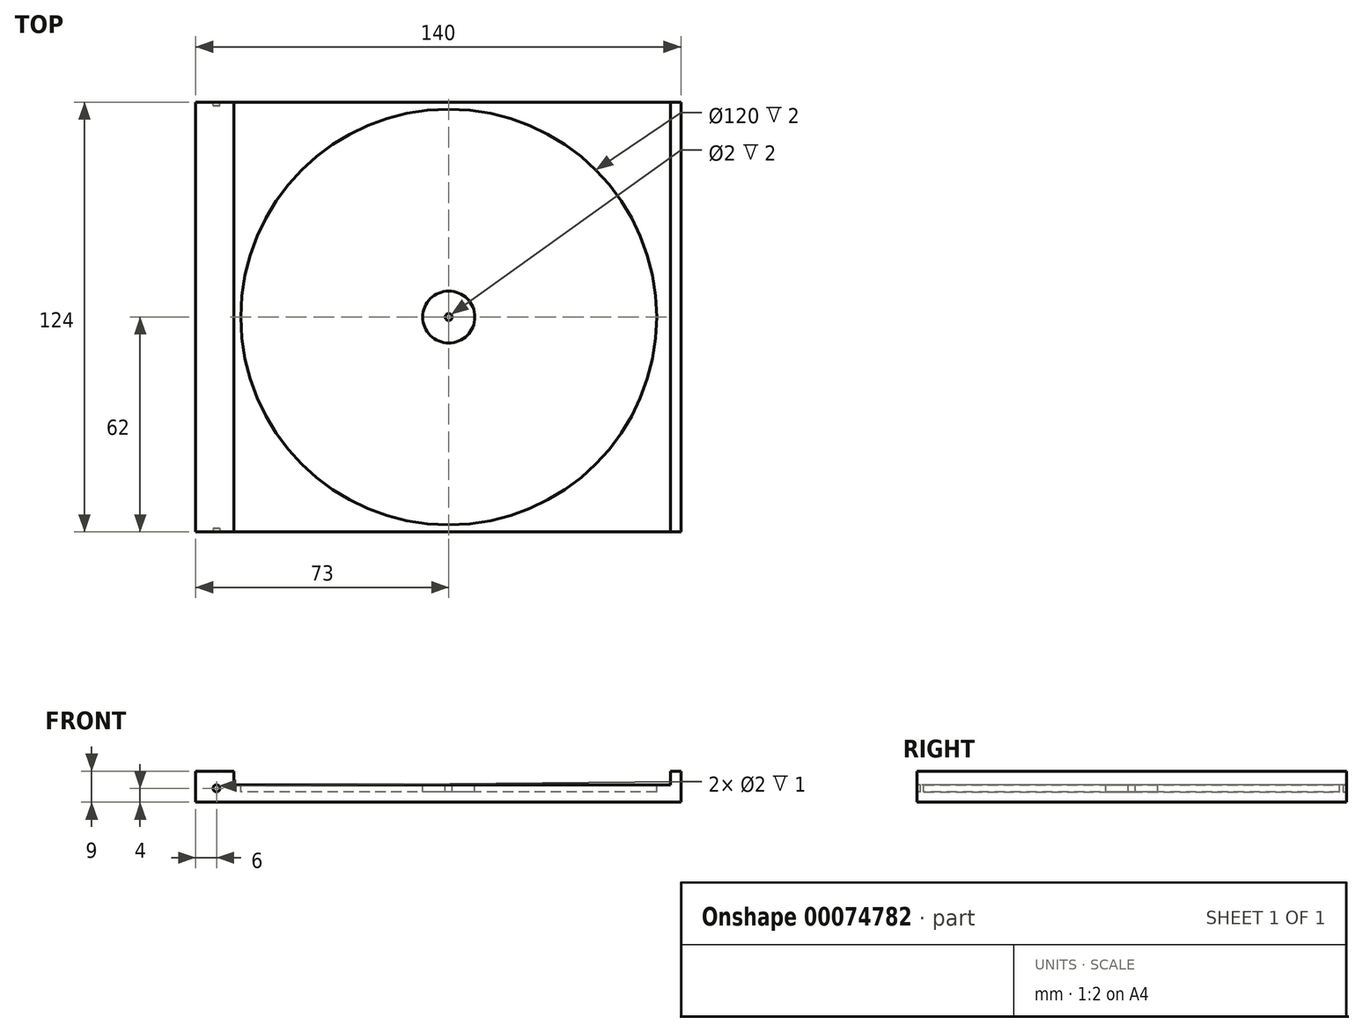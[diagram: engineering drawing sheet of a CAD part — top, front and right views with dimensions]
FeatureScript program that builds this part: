
annotation { "Feature Type Name" : "Feature", "Feature Type Description" : "" }
export const myFeature = defineFeature(function(context is Context, id is Id, definition is map)
    precondition{}
    {
        {
            var Q0;
            Q0=qCreatedBy(makeId("Top.planeOp"),FACE);
            var sketch = newSketch(context, id + "F0", { "sketchPlane" : qUnion([Q0])});
            skLineSegment(sketch, "E0.rect.bottom", {"start": v(-70, 62) * mm, "end": v(70, 62) * mm});
            skLineSegment(sketch, "E0.rect.top", {"start": v(-70, -62) * mm, "end": v(70, -62) * mm});
            skLineSegment(sketch, "E0.rect.left", {"start": v(-70, 62) * mm, "end": v(-70, -62) * mm});
            skLineSegment(sketch, "E0.rect.right", {"start": v(70, 62) * mm, "end": v(70, -62) * mm});
            skPoint(sketch, "E0.rect.middle", {"position": v(0, 0) * mm});
            skSolve(sketch);
        }
        {
            var Q0;
            Q0 = qSketchRegion(id + "F0", true);
            extrude(context, id + "F1", {"entities" : qUnion([Q0]), "oppositeDirection" : true, "depth" : 5 * mm});
        }
        {
            var Q0;
            Q0=makeQuery(id+"F1.opExtrude","CAP_FACE",FACE,{"disambiguationData":[OSD([sQuery(id+"F0.wireOp",EDGE,"E0.rect.bottom"),sQuery(id+"F0.wireOp",EDGE,"E0.rect.top"),sQuery(id+"F0.wireOp",EDGE,"E0.rect.left"),sQuery(id+"F0.wireOp",EDGE,"E0.rect.right")])],"isStart":true});
            var sketch = newSketch(context, id + "F2", { "sketchPlane" : qUnion([Q0])});
            skLineSegment(sketch, "E1", {"start": v(-59, -62) * mm, "end": v(-59, 62) * mm});
            skLineSegment(sketch, "E2", {"start": v(67, 62) * mm, "end": v(67, -62) * mm});
            skPoint(sketch, "E3.endSnap0", {"position": v(70, 0) * mm});
            skLineSegment(sketch, "E4", {"start": v(-59, 62) * mm, "end": v(-70, 62) * mm});
            skLineSegment(sketch, "E5", {"start": v(-70, 62) * mm, "end": v(-70, -62) * mm});
            skLineSegment(sketch, "E6", {"start": v(-70, -62) * mm, "end": v(-59, -62) * mm});
            skLineSegment(sketch, "E7", {"start": v(67, 62) * mm, "end": v(70, 62) * mm});
            skLineSegment(sketch, "E8", {"start": v(70, 62) * mm, "end": v(70, -62) * mm});
            skLineSegment(sketch, "E9", {"start": v(70, -62) * mm, "end": v(67, -62) * mm});
            skSolve(sketch);
        }
        {
            var Q0;
            Q0 = qSketchRegion(id + "F2", true);
            extrude(context, id + "F3", {"entities" : qUnion([Q0]), "operationType" : NewBodyOperationType.ADD, "depth" : 4 * mm});
        }
        {
            var Q0;
            Q0=makeQuery(id+"F1.opExtrude","CAP_FACE",FACE,{"disambiguationData":[OSD([sQuery(id+"F0.wireOp",EDGE,"E0.rect.bottom"),sQuery(id+"F0.wireOp",EDGE,"E0.rect.top"),sQuery(id+"F0.wireOp",EDGE,"E0.rect.left"),sQuery(id+"F0.wireOp",EDGE,"E0.rect.right")])],"isStart":true});
            var sketch = newSketch(context, id + "F4", { "sketchPlane" : qUnion([Q0])});
            skLineSegment(sketch, "E10.0", {"start": v(-59, 0) * mm, "end": v(67, 0) * mm});
            skLineSegment(sketch, "E11.0", {"start": v(3, 62) * mm, "end": v(3, -62) * mm});
            skCircle(sketch, "E12", {"center": v(3, 0) * mm, "radius": 60 * mm});
            skCircle(sketch, "E13", {"center": v(3, 0) * mm, "radius": 7.5 * mm});
            skCircle(sketch, "E14", {"center": v(3, 0) * mm, "radius": 1 * mm});
            skSolve(sketch);
        }
        {
            var Q0;
            Q0 = qSketchRegion(id + "F4", true);
            extrude(context, id + "F5", {"entities" : qUnion([Q0]), "operationType" : NewBodyOperationType.REMOVE, "flatOperationType" : FlatOperationType.REMOVE, "oppositeDirection" : true, "offsetDistance" : 25 * mm, "depth" : 2 * mm, "domain" : OperationDomain.MODEL});
        }
        {
            var Q0;
            {var subQ0=sQuery(id+"F4.wireOp",EDGE,"E11.0");var subQ1=sQuery(id+"F4.wireOp",EDGE,"E10.0");var subQ2=makeQuery(id+"F4.imprint","INTERSECT",VERTEX,{"derivedFrom":[subQ1,subQ0]});Q0=makeQuery(id+"F4.imprint","IMPRINT",FACE,{"disambiguationData":[TD([[makeQuery(id+"F4.imprint","IMPRINT",EDGE,{"disambiguationData":[TD([[subQ2,-1.0]])],"derivedFrom":subQ1}),-1.0]])]});}
            var Q1;
            {var subQ0=sQuery(id+"F4.wireOp",EDGE,"E14");var subQ1=sQuery(id+"F4.wireOp",EDGE,"E10.0");var subQ2=makeQuery(id+"F4.imprint","INTERSECT",VERTEX,{"disambiguationData":[OD(0.0)],"derivedFrom":[subQ1,subQ0]});Q1=makeQuery(id+"F4.imprint","IMPRINT",FACE,{"disambiguationData":[TD([[makeQuery(id+"F4.imprint","IMPRINT",EDGE,{"disambiguationData":[TD([[subQ2,-1.0]])],"derivedFrom":subQ1}),-1.0]])]});}
            var Q2;
            {var subQ0=sQuery(id+"F4.wireOp",EDGE,"E14");var subQ1=sQuery(id+"F4.wireOp",EDGE,"E10.0");var subQ2=makeQuery(id+"F4.imprint","INTERSECT",VERTEX,{"disambiguationData":[OD(0.0)],"derivedFrom":[subQ1,subQ0]});Q2=makeQuery(id+"F4.imprint","IMPRINT",FACE,{"disambiguationData":[TD([[makeQuery(id+"F4.imprint","IMPRINT",EDGE,{"disambiguationData":[TD([[subQ2,-1.0]])],"derivedFrom":subQ1}),1.0]])]});}
            var Q3;
            {var subQ0=sQuery(id+"F4.wireOp",EDGE,"E11.0");var subQ1=sQuery(id+"F4.wireOp",EDGE,"E10.0");var subQ2=makeQuery(id+"F4.imprint","INTERSECT",VERTEX,{"derivedFrom":[subQ1,subQ0]});Q3=makeQuery(id+"F4.imprint","IMPRINT",FACE,{"disambiguationData":[TD([[makeQuery(id+"F4.imprint","IMPRINT",EDGE,{"disambiguationData":[TD([[subQ2,-1.0]])],"derivedFrom":subQ1}),1.0]])]});}
            var Q4;
            Q4=sQuery(id+"F4.wireOp",EDGE,"E14");
            extrude(context, id + "F6", {"entities" : qUnion([Q0, Q1, Q2, Q3]), "operationType" : NewBodyOperationType.REMOVE, "surfaceEntities" : qUnion([Q4]), "oppositeDirection" : true, "depth" : 2 * mm});
        }
        {
            var Q0;
            Q0=makeQuery(id+"F3.boolean.opBoolean","MERGE",FACE,{"derivedFrom":[makeQuery(id+"F1.opExtrude","SWEPT_FACE",FACE,{"disambiguationData":[OSD([sQuery(id+"F0.wireOp",EDGE,"E0.rect.bottom")])]}),makeQuery(id+"F3.opExtrude","SWEPT_FACE",FACE,{"disambiguationData":[OSD([sQuery(id+"F2.wireOp",EDGE,"E4")])]}),makeQuery(id+"F3.opExtrude","SWEPT_FACE",FACE,{"disambiguationData":[OSD([sQuery(id+"F2.wireOp",EDGE,"E7")])]})]});
            var sketch = newSketch(context, id + "F7", { "sketchPlane" : qUnion([Q0])});
            skCircle(sketch, "E15", {"center": v(64, -1) * mm, "radius": 1 * mm});
            skSolve(sketch);
        }
        {
            var Q0;
            Q0 = qSketchRegion(id + "F7", true);
            extrude(context, id + "F8", {"entities" : qUnion([Q0]), "operationType" : NewBodyOperationType.REMOVE, "oppositeDirection" : true, "depth" : 1 * mm});
        }
        {
            var Q0;
            Q0=makeQuery(id+"F3.boolean.opBoolean","MERGE",FACE,{"derivedFrom":[makeQuery(id+"F1.opExtrude","SWEPT_FACE",FACE,{"disambiguationData":[OSD([sQuery(id+"F0.wireOp",EDGE,"E0.rect.top")])]}),makeQuery(id+"F3.opExtrude","SWEPT_FACE",FACE,{"disambiguationData":[OSD([sQuery(id+"F2.wireOp",EDGE,"E6")])]}),makeQuery(id+"F3.opExtrude","SWEPT_FACE",FACE,{"disambiguationData":[OSD([sQuery(id+"F2.wireOp",EDGE,"E9")])]})]});
            var sketch = newSketch(context, id + "F9", { "sketchPlane" : qUnion([Q0])});
            skCircle(sketch, "E16", {"center": v(-64, -1) * mm, "radius": 1 * mm});
            skSolve(sketch);
        }
        {
            var Q0;
            Q0 = qSketchRegion(id + "F9", true);
            extrude(context, id + "F10", {"entities" : qUnion([Q0]), "operationType" : NewBodyOperationType.REMOVE, "oppositeDirection" : true, "depth" : 1 * mm});
        }
    });
